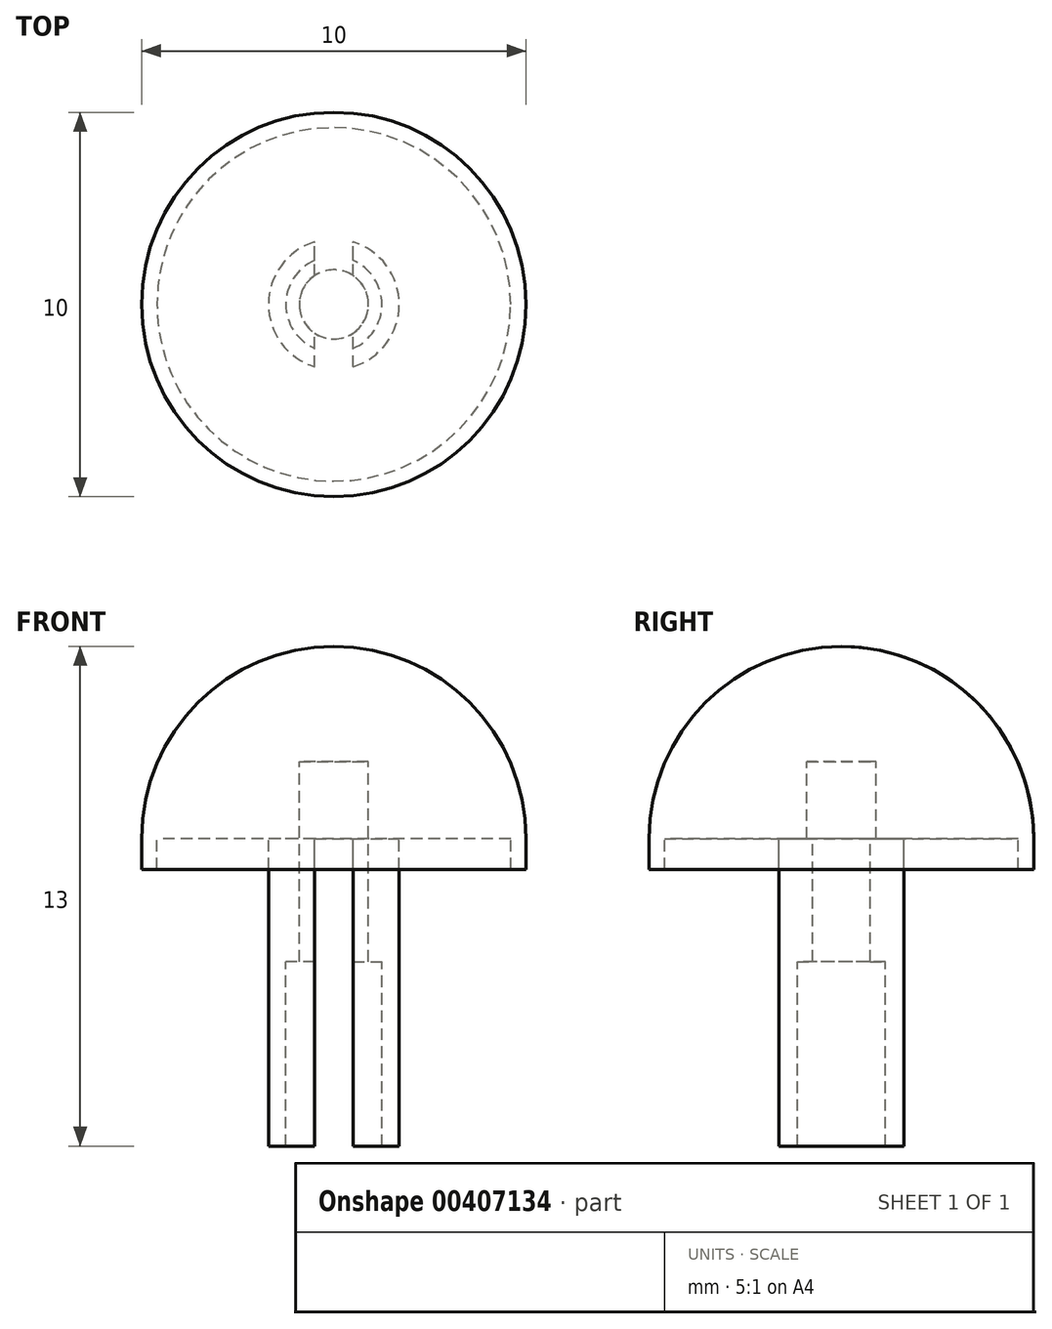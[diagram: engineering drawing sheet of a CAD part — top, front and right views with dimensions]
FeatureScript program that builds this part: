
annotation { "Feature Type Name" : "Feature", "Feature Type Description" : "" }
export const myFeature = defineFeature(function(context is Context, id is Id, definition is map)
    precondition{}
    {
        {
            var Q0;
            Q0=qCreatedBy(makeId("Right.planeOp"),FACE);
            var sketch = newSketch(context, id + "F0", { "sketchPlane" : qUnion([Q0])});
            skArc(sketch, "E0", {"start": v(5, 0) * mm, "mid": v(3.54, 3.54) * mm, "end": v(0, 5) * mm});
            skPoint(sketch, "E1.visualSharp", {"position": v(5, 0) * mm});
            skLineSegment(sketch, "E2", {"start": v(1.7, 0) * mm, "end": v(4.6, 0) * mm});
            skLineSegment(sketch, "E3", {"start": v(1.7, 0) * mm, "end": v(1.7, -8) * mm});
            skLineSegment(sketch, "E4", {"start": v(1.7, -8) * mm, "end": v(0, -8) * mm});
            skLineSegment(sketch, "E5", {"start": v(0, 5) * mm, "end": v(0, -8) * mm});
            skLineSegment(sketch, "E6", {"start": v(0, 5.15) * mm, "end": v(0, -4.66) * mm, "construction": true});
            skLineSegment(sketch, "E7.top", {"start": v(4.6, -0.8) * mm, "end": v(5, -0.8) * mm});
            skLineSegment(sketch, "E7.left", {"start": v(4.6, 0) * mm, "end": v(4.6, -0.8) * mm});
            skLineSegment(sketch, "E7.right", {"start": v(5, 0) * mm, "end": v(5, -0.8) * mm});
            skSolve(sketch);
        }
        {
            var Q0;
            Q0=qSketchRegion(id+"F0",true);
            var Q1;
            Q1=sQuery(id+"F0.wireOp",EDGE,"E0");
            var Q2;
            Q2=sQuery(id+"F0.wireOp",EDGE,"UYL8Wqyh-qlkQ-H2Dr-IV88-MgrWhvk87JcP");
            var Q3;
            Q3=sQuery(id+"F0.wireOp",EDGE,"E1.filletArc");
            var Q4;
            Q4=sQuery(id+"F0.wireOp",EDGE,"E5");
            revolve(context, id + "F1", {"entities" : qUnion([Q0]), "surfaceEntities" : qUnion([Q1, Q2, Q3]), "axis" : qUnion([Q4]), "revolveType" : RevolveType.FULL});
        }
        {
            var Q0;
            Q0=qCreatedBy(makeId("Top.planeOp"),FACE);
            var sketch = newSketch(context, id + "F2", { "sketchPlane" : qUnion([Q0])});
            skCircle(sketch, "E8", {"center": v(0, 0) * mm, "radius": 1.25 * mm});
            skSolve(sketch);
        }
        {
            var Q0;
            Q0 = qSketchRegion(id + "F2", true);
            extrude(context, id + "F3", {"entities" : qUnion([Q0]), "operationType" : NewBodyOperationType.REMOVE, "endBound" : BoundingType.THROUGH_ALL, "oppositeDirection" : true, "depth" : 10 * mm});
        }
        {
            var Q0;
            Q0=qCreatedBy(makeId("Top.planeOp"),FACE);
            var sketch = newSketch(context, id + "F4", { "sketchPlane" : qUnion([Q0])});
            skCircle(sketch, "E9", {"center": v(0, 0) * mm, "radius": 1.5 * mm});
            skSolve(sketch);
        }
        {
            var Q0;
            Q0=makeQuery(id+"F1.opRevolve","SWEPT_FACE",FACE,{"disambiguationData":[OSD([sQuery(id+"F0.wireOp",EDGE,"E2")])]});
            var sketch = newSketch(context, id + "F5", { "sketchPlane" : qUnion([Q0])});
            skCircle(sketch, "E10", {"center": v(0, 0) * mm, "radius": 0.9 * mm});
            skCircle(sketch, "E11.0", {"center": v(0, 0) * mm, "radius": 1.25 * mm});
            skSolve(sketch);
        }
        {
            var Q0;
            Q0 = qSketchRegion(id + "F5", true);
            extrude(context, id + "F6", {"entities" : qUnion([Q0]), "operationType" : NewBodyOperationType.ADD, "depth" : 3.2 * mm});
        }
        {
            var Q0;
            Q0=makeQuery(id+"F1.opRevolve","SWEPT_FACE",FACE,{"disambiguationData":[OSD([sQuery(id+"F0.wireOp",EDGE,"E4")])]});
            var sketch = newSketch(context, id + "F7", { "sketchPlane" : qUnion([Q0])});
            skLineSegment(sketch, "E12.bottom", {"start": v(-0.5, 2) * mm, "end": v(0.5, 2) * mm});
            skLineSegment(sketch, "E12.top", {"start": v(-0.5, -2) * mm, "end": v(0.5, -2) * mm});
            skLineSegment(sketch, "E12.left", {"start": v(-0.5, 2) * mm, "end": v(-0.5, -2) * mm});
            skLineSegment(sketch, "E12.right", {"start": v(0.5, 2) * mm, "end": v(0.5, -2) * mm});
            skLineSegment(sketch, "E13", {"start": v(0, 2.44) * mm, "end": v(0, -2.43) * mm, "construction": true});
            skSolve(sketch);
        }
        {
            var Q0;
            Q0 = qSketchRegion(id + "F7", true);
            var Q1;
            Q1=makeQuery(id+"F1.opRevolve","SWEPT_FACE",FACE,{"disambiguationData":[OSD([sQuery(id+"F0.wireOp",EDGE,"E2")])]});
            extrude(context, id + "F8", {"entities" : qUnion([Q0]), "operationType" : NewBodyOperationType.REMOVE, "endBound" : BoundingType.UP_TO_SURFACE, "oppositeDirection" : true, "endBoundEntityFace" : qUnion([Q1]), "depth" : 25 * mm});
        }
        {
            var Q0;
            {var subQ0=sQuery(id+"F0.wireOp",EDGE,"E2");Q0=makeQuery(id+"F8.boolean.opBoolean","MERGE",FACE,{"derivedFrom":[makeQuery(id+"F1.opRevolve","SWEPT_FACE",FACE,{"disambiguationData":[OSD([subQ0])]}),makeQuery(id+"F3.boolean.opBoolean","COPY",FACE,{"derivedFrom":makeQuery(id+"F3.opExtrude","CAP_FACE",FACE,{"disambiguationData":[OSD([sQuery(id+"F2.wireOp",EDGE,"E8")])],"isStart":true})}),makeQuery(id+"F8.opExtrude","CAP_FACE",FACE,{"disambiguationData":[OSD([subQ0])],"isStart":false})]});}
            var sketch = newSketch(context, id + "F9", { "sketchPlane" : qUnion([Q0])});
            skArc(sketch, "E14.0", {"start": v(-0.5, 0.75) * mm, "mid": v(-0.9, 0) * mm, "end": v(-0.5, -0.75) * mm, "construction": true});
            skCircle(sketch, "E15", {"center": v(0, 0) * mm, "radius": 0.9 * mm});
            skSolve(sketch);
        }
        {
            var Q0;
            Q0 = qSketchRegion(id + "F9", true);
            extrude(context, id + "F10", {"entities" : qUnion([Q0]), "operationType" : NewBodyOperationType.REMOVE, "oppositeDirection" : true, "depth" : 2 * mm});
        }
    });
